# Revit family: РИДАН_Кран шаровой BVS-FR из нержавеющей стали
name_source: partatom
category: Арматура трубопроводов
units: mm (PartAtom-declared; Revit-internal decimal feet)

## family parameters
Всегда вертикально = Да
На основе рабочей плоскости = Нет
Общий = Нет
При загрузке вырезать с полостями = Нет
Размер круглого соединителя = Использовать диаметр
Тип детали = Вставляется

## types (11) — shared parameters
ADSK_Версия Revit = 2019
ADSK_Версия семейства = 1.0
ADSK_Единица измерения = шт.
ADSK_Завод-изготовитель = ООО «Ридан-Трейд»
ADSK_Количество = 1
ADSK_Потеря давления жидкости = 0.0 Па
ADSK_Расход жидкости = 0.000 м³/ч
LT = BVS-FR
URL = https://ridan.ru
Изготовитель = ООО «Ридан-Трейд»

## per-type parameters (varying)
| type | ADSK_Диаметр условный | ADSK_Код изделия | ADSK_Марка | ADSK_Масса | ADSK_Наименование | ADSK_Пропускная способность | a | b | c | d | e | f | g | h | i | j | k |
| DN 8 | 8 мм | 082X4610R | BVS-FR DN8 | 0.23 | Кран шаровой BVS-FR полнопроходной из нержавеющей стали PN63, Tmax=180C, ВР, DN8 | 6.000 м³/ч | 10 мм | 15 мм | 13 мм | 11 мм | 29 мм | 31 мм | 17 мм | 23 мм | 22 мм | 120 мм | 15 мм |
| DN 10 | 10 мм | 082X4611R | BVS-FR DN10 | 0.23 | Кран шаровой BVS-FR полнопроходной из нержавеющей стали PN63, Tmax=180C, ВР, DN10 | 16.000 м³/ч | 10 мм | 15 мм | 13 мм | 11 мм | 29 мм | 31 мм | 17 мм | 23 мм | 22 мм | 120 мм | 17 мм |
| DN 15 | 15 мм | 082X4612R | BVS-FR DN15 | 0.24 | Кран шаровой BVS-FR полнопроходной из нержавеющей стали PN63, Tmax=180C, ВР, DN15 | 35.000 м³/ч | 10 мм | 17 мм | 16 мм | 12 мм | 29 мм | 35 мм | 17 мм | 26 мм | 26 мм | 121 мм | 21 мм |
| DN 20 | 20 мм | 082X4613R | BVS-FR DN20 | 0.45 | Кран шаровой BVS-FR полнопроходной из нержавеющей стали PN63, Tmax=180C, ВР, DN20 | 46.000 м³/ч | 12 мм | 20 мм | 18 мм | 14 мм | 37 мм | 42 мм | 17 мм | 33 мм | 32 мм | 120 мм | 26 мм |
| DN 25 | 25 мм | 082X4614R | BVS-FR DN25 | 0.65 | Кран шаровой BVS-FR полнопроходной из нержавеющей стали PN63, Tmax=180C, ВР, DN25 | 72.000 м³/ч | 16 мм | 25 мм | 22 мм | 20 мм | 42 мм | 50 мм | 21 мм | 39 мм | 39 мм | 121 мм | 34 мм |
| DN 32 | 32 мм | 082X4615R | BVS-FR DN32 | 1.05 | Кран шаровой BVS-FR полнопроходной из нержавеющей стали PN63, Tmax=180C, ВР, DN32 | 105.000 м³/ч | 18 мм | 27 мм | 24 мм | 21 мм | 50 мм | 63 мм | 22 мм | 51 мм | 49 мм | 119 мм | 42 мм |
| DN 40 | 40 мм | 082X4616R | BVS-FR DN40 | 1.7 | Кран шаровой BVS-FR полнопроходной из нержавеющей стали PN63, Tmax=180C, ВР, DN40 | 170.000 м³/ч | 22 мм | 31 мм | 30 мм | 23 мм | 60 мм | 76 мм | 25 мм | 57 мм | 55 мм | 119 мм | 48 мм |
| DN 50 | 50 мм | 082X4617R | BVS-FR DN50 | 2.61 | Кран шаровой BVS-FR полнопроходной из нержавеющей стали PN63, Tmax=180C, ВР, DN50 | 275.000 м³/ч | 25 мм | 37 мм | 38 мм | 24 мм | 68 мм | 91 мм | 23 мм | 70 мм | 68 мм | 120 мм | 60 мм |
| DN 65 | 65 мм | 082X4618R | BVS-FR DN65 | 5.01 | Кран шаровой BVS-FR полнопроходной из нержавеющей стали PN63, Tmax=180C, ВР, DN65 | 507.000 м³/ч | 31 мм | 45 мм | 42 мм | 35 мм | 90 мм | 113 мм | 32 мм | 85 мм | 85 мм | 120 мм | 76 мм |
| DN 80 | 80 мм | 082X4619R | BVS-FR DN80 | 7.61 | Кран шаровой BVS-FR полнопроходной из нержавеющей стали PN63, Tmax=180C, ВР, DN80 | 905.000 м³/ч | 35 мм | 51 мм | 49 мм | 38 мм | 99 мм | 133 мм | 32 мм | 100 мм | 100 мм | 120 мм | 89 мм |
| DN 100 | 100 мм | 082X4620R | BVS-FR DN100 | 14.75 | Кран шаровой BVS-FR полнопроходной из нержавеющей стали PN63, Tmax=180C, ВР, DN100 | 1000.000 м³/ч | 39 мм | 72 мм | 54 мм | 57 мм | 122 мм | 159 мм | 43 мм | 128 мм | 128 мм | 119 мм | 108 мм |
